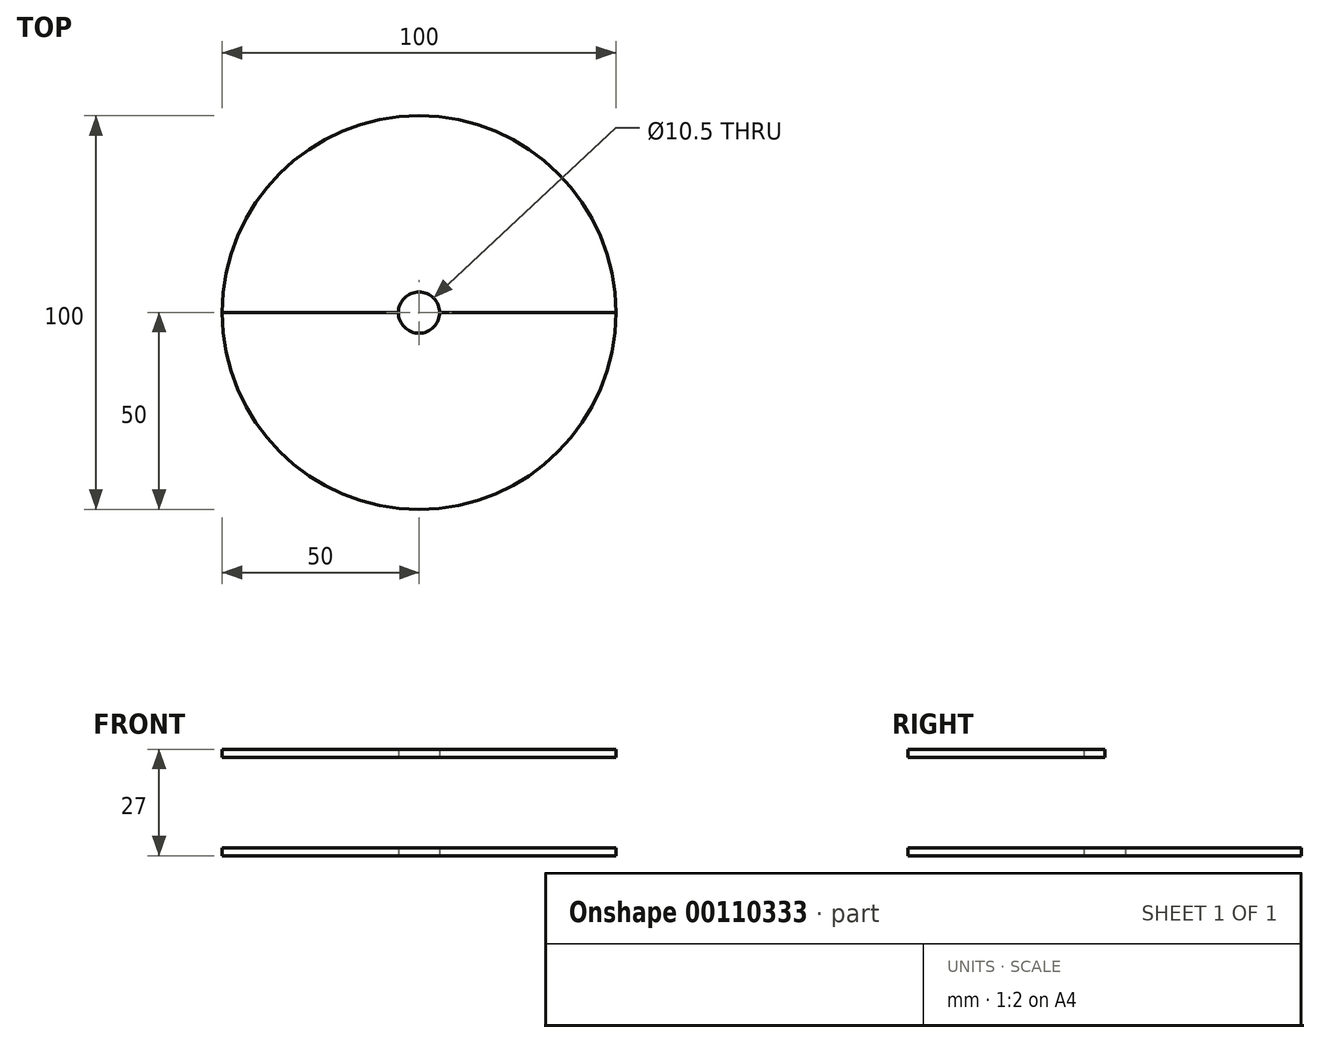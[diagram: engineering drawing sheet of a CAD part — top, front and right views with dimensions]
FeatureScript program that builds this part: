
annotation { "Feature Type Name" : "Feature", "Feature Type Description" : "" }
export const myFeature = defineFeature(function(context is Context, id is Id, definition is map)
    precondition{}
    {
        {
            var Q0;
            Q0=qCreatedBy(makeId("Top.planeOp"),FACE);
            var sketch = newSketch(context, id + "F0", { "sketchPlane" : qUnion([Q0])});
            skCircle(sketch, "E0", {"center": v(0, 0) * mm, "radius": 50 * mm});
            skCircle(sketch, "E1", {"center": v(0, 0) * mm, "radius": 5.25 * mm});
            skLineSegment(sketch, "E2", {"start": v(0, 0) * mm, "end": v(-50, 0) * mm});
            skLineSegment(sketch, "E3", {"start": v(-50, 0) * mm, "end": v(50, 0) * mm});
            skSolve(sketch);
        }
        {
            var Q0;
            Q0=qCreatedBy(makeId("Top.planeOp"),FACE);
            cPlane(context, id + "F1", {"entities" : qUnion([Q0]), "cplaneType" : CPlaneType.OFFSET, "offset" : 25 * mm, "width" : 150 * mm, "height" : 150 * mm});
        }
        {
            var Q0;
            Q0=qCreatedBy(id+"F1.planeOp",FACE);
            var sketch = newSketch(context, id + "F2", { "sketchPlane" : qUnion([Q0])});
            skLineSegment(sketch, "E4.0.0", {"start": v(-5.25, 0) * mm, "end": v(-50, 0) * mm});
            skArc(sketch, "E4.0.1", {"start": v(-50, 0) * mm, "mid": v(0, -50) * mm, "end": v(50, 0) * mm});
            skLineSegment(sketch, "E4.0.2", {"start": v(50, 0) * mm, "end": v(5.25, 0) * mm});
            skArc(sketch, "E4.0.3", {"start": v(5.25, 0) * mm, "mid": v(0, -5.25) * mm, "end": v(-5.25, 0) * mm});
            skSolve(sketch);
        }
        {
            var Q0;
            Q0=makeQuery(id+"F2.imprint","IMPRINT",FACE,{"disambiguationData":[TD([[makeQuery(id+"F2.imprint","IMPRINT",EDGE,{"derivedFrom":sQuery(id+"F2.wireOp",EDGE,"E4.0.0")}),1.0]])]});
            extrude(context, id + "F3", {"entities" : qUnion([Q0]), "depth" : 2 * mm});
        }
        {
            var Q0;
            {var subQ0=sQuery(id+"F0.wireOp",EDGE,"E3");var subQ1=sQuery(id+"F0.wireOp",EDGE,"E0");var subQ2=makeQuery(id+"F0.imprint","INTERSECT",VERTEX,{"disambiguationData":[OD(0.0)],"derivedFrom":[subQ1,subQ0]});Q0=makeQuery(id+"F0.imprint","IMPRINT",FACE,{"disambiguationData":[TD([[makeQuery(id+"F0.imprint","IMPRINT",EDGE,{"disambiguationData":[TD([[subQ2,-1.0]])],"derivedFrom":subQ1}),1.0]])]});}
            var Q1;
            {var subQ0=sQuery(id+"F0.wireOp",EDGE,"E3");var subQ1=sQuery(id+"F0.wireOp",EDGE,"E0");var subQ2=makeQuery(id+"F0.imprint","INTERSECT",VERTEX,{"disambiguationData":[OD(0.0)],"derivedFrom":[subQ1,subQ0]});Q1=makeQuery(id+"F0.imprint","IMPRINT",FACE,{"disambiguationData":[TD([[makeQuery(id+"F0.imprint","IMPRINT",EDGE,{"disambiguationData":[TD([[subQ2,1.0]])],"derivedFrom":subQ1}),1.0]])]});}
            extrude(context, id + "F4", {"entities" : qUnion([Q0, Q1]), "depth" : 2 * mm});
        }
    });
